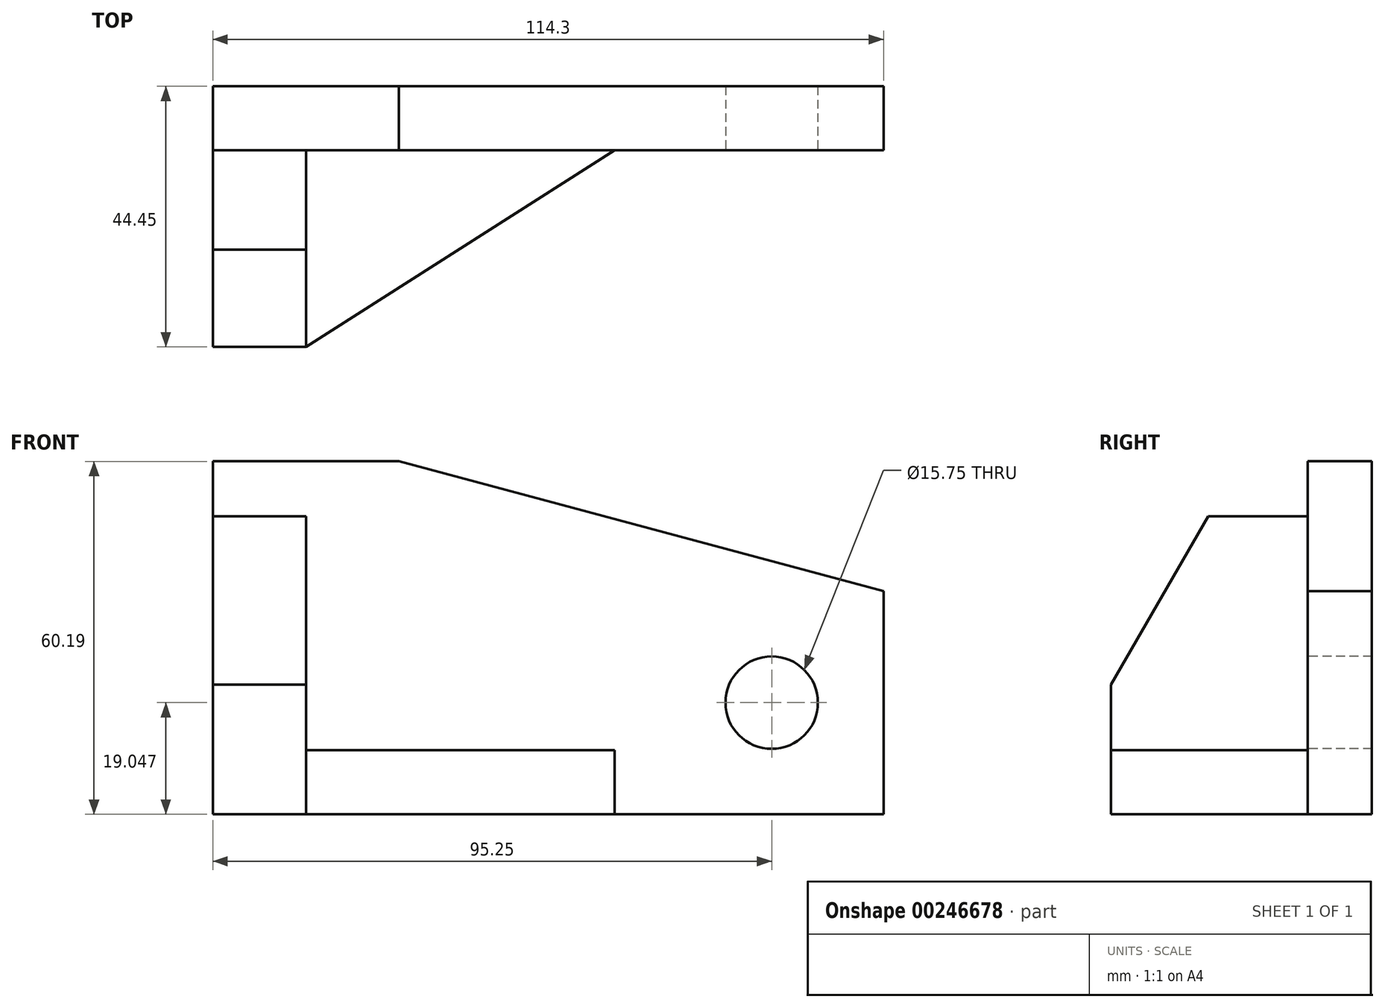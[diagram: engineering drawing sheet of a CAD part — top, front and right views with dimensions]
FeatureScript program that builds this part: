
annotation { "Feature Type Name" : "Feature", "Feature Type Description" : "" }
export const myFeature = defineFeature(function(context is Context, id is Id, definition is map)
    precondition{}
    {
        {
            var Q0;
            Q0=qCreatedBy(makeId("Front.planeOp"),FACE);
            var sketch = newSketch(context, id + "F0", { "sketchPlane" : qUnion([Q0])});
            skLineSegment(sketch, "E0.bottom", {"start": v(-57.15, 29.6) * mm, "end": v(57.15, 29.6) * mm});
            skLineSegment(sketch, "E0.top", {"start": v(-57.15, -30.6) * mm, "end": v(57.15, -30.6) * mm});
            skLineSegment(sketch, "E0.left", {"start": v(-57.15, 29.6) * mm, "end": v(-57.15, -30.6) * mm});
            skLineSegment(sketch, "E0.right", {"start": v(57.15, 29.6) * mm, "end": v(57.15, -30.6) * mm});
            skPoint(sketch, "E1", {"position": v(-25.4, 29.6) * mm});
            skLineSegment(sketch, "E2", {"start": v(-25.4, 29.6) * mm, "end": v(57.15, 7.48) * mm});
            skSolve(sketch);
        }
        {
            var Q0;
            {var subQ1=sQuery(id+"F0.wireOp",EDGE,"E0.top");Q0=makeQuery(id+"F0.imprint","IMPRINT",FACE,{"disambiguationData":[TD([[makeQuery(id+"F0.imprint","IMPRINT",EDGE,{"derivedFrom":subQ1}),1.0]])]});}
            extrude(context, id + "F1", {"entities" : qUnion([Q0]), "depth" : 10.92 * mm});
        }
        {
            var Q0;
            Q0=makeQuery(id+"F1.opExtrude","CAP_FACE",FACE,{"disambiguationData":[OSD([sQuery(id+"F0.wireOp",EDGE,"E0.bottom"),sQuery(id+"F0.wireOp",EDGE,"E0.top"),sQuery(id+"F0.wireOp",EDGE,"E0.left"),sQuery(id+"F0.wireOp",EDGE,"E0.right"),sQuery(id+"F0.wireOp",EDGE,"E2")])],"isStart":false});
            var sketch = newSketch(context, id + "F2", { "sketchPlane" : qUnion([Q0])});
            skLineSegment(sketch, "E3.bottom", {"start": v(-57.15, 20.2) * mm, "end": v(-41.27, 20.2) * mm});
            skLineSegment(sketch, "E3.top", {"start": v(-57.15, -30.6) * mm, "end": v(-41.27, -30.6) * mm});
            skLineSegment(sketch, "E3.left", {"start": v(-57.15, 20.2) * mm, "end": v(-57.15, -30.6) * mm});
            skLineSegment(sketch, "E3.right", {"start": v(-41.27, 20.2) * mm, "end": v(-41.27, -30.6) * mm});
            skSolve(sketch);
        }
        {
            var Q0;
            Q0=makeQuery(id+"F2.imprint","IMPRINT",FACE,{"disambiguationData":[TD([[makeQuery(id+"F2.imprint","IMPRINT",EDGE,{"derivedFrom":sQuery(id+"F2.wireOp",EDGE,"E3.bottom")}),-1.0]])]});
            extrude(context, id + "F3", {"entities" : qUnion([Q0]), "operationType" : NewBodyOperationType.ADD, "depth" : 33.53 * mm});
        }
        {
            var Q0;
            Q0=makeQuery(id+"F3.opExtrude","SWEPT_FACE",FACE,{"disambiguationData":[OSD([sQuery(id+"F2.wireOp",EDGE,"E3.right")])]});
            var sketch = newSketch(context, id + "F4", { "sketchPlane" : qUnion([Q0])});
            skLineSegment(sketch, "E4", {"start": v(-27.88, 20.2) * mm, "end": v(-44.45, -8.5) * mm});
            skSolve(sketch);
        }
        {
            var Q0;
            Q0 = qSketchRegion(id + "F4", true);
            var Q1;
            {var subQ0=sQuery(id+"F4.wireOp",EDGE,"E4");Q1=makeQuery(id+"F4.imprint","IMPRINT",FACE,{"disambiguationData":[TD([[makeQuery(id+"F4.imprint","IMPRINT",EDGE,{"derivedFrom":subQ0}),-1.0]])]});}
            extrude(context, id + "F5", {"entities" : qUnion([Q0, Q1]), "operationType" : NewBodyOperationType.REMOVE, "oppositeDirection" : true, "depth" : 25.4 * mm});
        }
        {
            var Q0;
            Q0=makeQuery(id+"F1.opExtrude","CAP_FACE",FACE,{"disambiguationData":[OSD([sQuery(id+"F0.wireOp",EDGE,"E0.bottom"),sQuery(id+"F0.wireOp",EDGE,"E0.top"),sQuery(id+"F0.wireOp",EDGE,"E0.left"),sQuery(id+"F0.wireOp",EDGE,"E0.right"),sQuery(id+"F0.wireOp",EDGE,"E2")])],"isStart":false});
            var sketch = newSketch(context, id + "F6", { "sketchPlane" : qUnion([Q0])});
            skLineSegment(sketch, "E5.bottom", {"start": v(-41.27, -19.68) * mm, "end": v(11.31, -19.68) * mm});
            skLineSegment(sketch, "E5.top", {"start": v(-41.27, -30.6) * mm, "end": v(11.31, -30.6) * mm});
            skLineSegment(sketch, "E5.left", {"start": v(-41.27, -19.68) * mm, "end": v(-41.27, -30.6) * mm});
            skLineSegment(sketch, "E5.right", {"start": v(11.31, -19.68) * mm, "end": v(11.31, -30.6) * mm});
            skSolve(sketch);
        }
        {
            var Q0;
            Q0=makeQuery(id+"F6.imprint","IMPRINT",FACE,{"disambiguationData":[TD([[makeQuery(id+"F6.imprint","IMPRINT",EDGE,{"derivedFrom":sQuery(id+"F6.wireOp",EDGE,"E5.bottom")}),-1.0]])]});
            extrude(context, id + "F7", {"entities" : qUnion([Q0]), "operationType" : NewBodyOperationType.ADD, "depth" : 33.53 * mm});
        }
        {
            var Q0;
            Q0=makeQuery(id+"F7.opExtrude","SWEPT_FACE",FACE,{"disambiguationData":[OSD([sQuery(id+"F6.wireOp",EDGE,"E5.bottom")])]});
            var sketch = newSketch(context, id + "F8", { "sketchPlane" : qUnion([Q0])});
            skLineSegment(sketch, "E6", {"start": v(-41.27, -44.45) * mm, "end": v(11.31, -10.92) * mm});
            skSolve(sketch);
        }
        {
            var Q0;
            Q0=makeQuery(id+"F8.imprint","IMPRINT",FACE,{"disambiguationData":[TD([[makeQuery(id+"F8.imprint","IMPRINT",EDGE,{"derivedFrom":sQuery(id+"F8.wireOp",EDGE,"E6")}),-1.0]])]});
            extrude(context, id + "F9", {"entities" : qUnion([Q0]), "operationType" : NewBodyOperationType.REMOVE, "oppositeDirection" : true, "depth" : 25.4 * mm});
        }
        {
            var Q0;
            Q0=makeQuery(id+"F1.opExtrude","CAP_FACE",FACE,{"disambiguationData":[OSD([sQuery(id+"F0.wireOp",EDGE,"E0.bottom"),sQuery(id+"F0.wireOp",EDGE,"E0.top"),sQuery(id+"F0.wireOp",EDGE,"E0.left"),sQuery(id+"F0.wireOp",EDGE,"E0.right"),sQuery(id+"F0.wireOp",EDGE,"E2")])],"isStart":false});
            var sketch = newSketch(context, id + "F10", { "sketchPlane" : qUnion([Q0])});
            skCircle(sketch, "E7", {"center": v(38.1, -11.55) * mm, "radius": 7.87 * mm});
            skSolve(sketch);
        }
        {
            var Q0;
            Q0=sQuery(id+"F10.wireOp",VERTEX,"E7.center");
            var Q1;
            Q1=makeQuery(id+"F1.opExtrude","SWEPT_BODY",BODY,{"disambiguationData":[OSD([sQuery(id+"F0.wireOp",EDGE,"E0.bottom"),sQuery(id+"F0.wireOp",EDGE,"E0.top"),sQuery(id+"F0.wireOp",EDGE,"E0.left"),sQuery(id+"F0.wireOp",EDGE,"E0.right"),sQuery(id+"F0.wireOp",EDGE,"E2")])]});
            hole(context, id + "F11", {"style" : HoleStyle.SIMPLE, "endStyle" : HoleEndStyle.THROUGH, "holeDiameter" : 15.75 * mm, "tappedDepth" : 12.7 * mm, "tapClearance" : 3, "locations" : qUnion([Q0]), "scope" : qUnion([Q1])});
        }
    });
